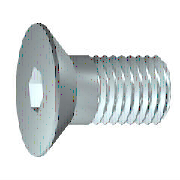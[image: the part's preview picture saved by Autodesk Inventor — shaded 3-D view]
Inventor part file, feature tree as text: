
AUTODESK INVENTOR PART (.ipt)
format: ipt  version: 2020 (Build 240168000, 168)  size: 188,416 bytes
history: native  units: mm (DEFAULTED — no unit token found)
features: other x4, sketch x3, fillet x1, chamfer x1
ambient origin geometry x8: Origin, YZ Plane, XZ Plane, XY Plane, X Axis, Y Axis, Z Axis, Center Point
bodies: Solid1 (feature_tree)
feature tree (9):
  sketch  "Sketch1"  dims[d2=3.0mm]
  other  "WorkPoint1"
  sketch  "Sketch2"  dims[d3=4.0mm]
  fillet  "Fillet1"  [1 undecoded]
  chamfer  "Chamfer1"  Distance=2.0mm
  other  "MSC_A1"
  other  "MSC_PF1"
  other  "MSC_PT1"
  sketch  "Sketch3"  dims[d4=1.5mm d5=2.0mm d6=8.0mm d7=20.0mm d8=360.0deg d9=0.0mm d10=2.0mm d11=2.5mm d12=120.0deg d13=120.0deg d14=120.0deg d15=120.0deg d16=1.8mm d17=0.0mm d18=0.2mm d19=0.35mm d20=45.0deg d22=0.0mm d23=0.0mm d35=0.0mm d37=0.0mm d38=0.0mm d39=0.35mm d40=0.0mm d41=0.0mm d42=0.0mm d43=45.0deg]
note: 1 required parameter value undecoded (feature->parameter linkage not recoverable at this tier; creation-order binding heuristic only, values carry confidence <= 0.55)
